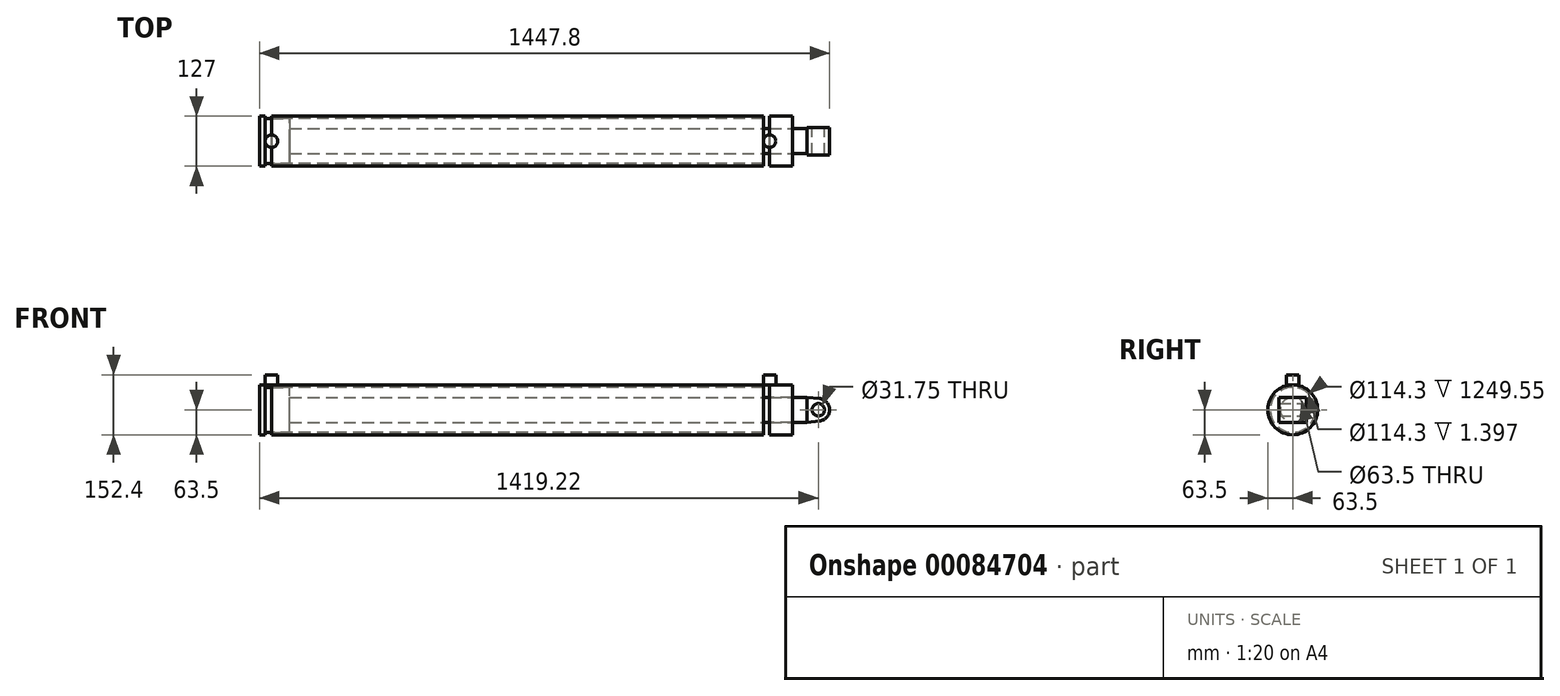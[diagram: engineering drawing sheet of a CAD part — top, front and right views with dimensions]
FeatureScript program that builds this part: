
annotation { "Feature Type Name" : "Feature", "Feature Type Description" : "" }
export const myFeature = defineFeature(function(context is Context, id is Id, definition is map)
    precondition{}
    {
        {
            var Q0;
            Q0=qCreatedBy(makeId("Front.planeOp"),FACE);
            var sketch = newSketch(context, id + "F0", { "sketchPlane" : qUnion([Q0])});
            skLineSegment(sketch, "E0.bottom", {"start": v(0, 0) * mm, "end": v(12.7, 0) * mm});
            skLineSegment(sketch, "E0.top", {"start": v(0, 63.5) * mm, "end": v(1353.31, 63.5) * mm});
            skLineSegment(sketch, "E0.left", {"start": v(0, 0) * mm, "end": v(0, 63.5) * mm});
            skLineSegment(sketch, "E0.right", {"start": v(1353.31, 31.75) * mm, "end": v(1353.31, 63.5) * mm});
            skLineSegment(sketch, "E1", {"start": v(12.7, 0) * mm, "end": v(12.7, 57.15) * mm});
            skLineSegment(sketch, "E2", {"start": v(12.7, 57.15) * mm, "end": v(1295.4, 57.15) * mm});
            skLineSegment(sketch, "E3", {"start": v(1295.4, 57.15) * mm, "end": v(1295.4, 31.75) * mm});
            skLineSegment(sketch, "E4", {"start": v(1295.4, 31.75) * mm, "end": v(1353.31, 31.75) * mm});
            skPoint(sketch, "E5.trimOffspring.start.orphan", {"position": v(1295.4, 0) * mm});
            skLineSegment(sketch, "E6", {"start": v(76.2, 57.15) * mm, "end": v(76.2, 31.75) * mm});
            skLineSegment(sketch, "E7", {"start": v(76.2, 31.75) * mm, "end": v(1390.65, 31.75) * mm});
            skLineSegment(sketch, "E8", {"start": v(1390.65, 31.75) * mm, "end": v(1390.65, 0) * mm});
            skLineSegment(sketch, "E9", {"start": v(1390.65, 0) * mm, "end": v(12.7, 0) * mm});
            skCircle(sketch, "E10", {"center": v(1419.23, 0) * mm, "radius": 28.58 * mm});
            skCircle(sketch, "E11", {"center": v(1419.23, 0) * mm, "radius": 15.88 * mm});
            skLineSegment(sketch, "E12", {"start": v(1422.22, 28.42) * mm, "end": v(1390.65, 31.75) * mm});
            skLineSegment(sketch, "E13", {"start": v(1390.65, 0) * mm, "end": v(1390.65, -31.75) * mm});
            skLineSegment(sketch, "E14", {"start": v(1390.65, -31.75) * mm, "end": v(1422.22, -28.42) * mm});
            skLineSegment(sketch, "E15.bottom", {"start": v(29.97, 57.15) * mm, "end": v(14.1, 57.15) * mm});
            skLineSegment(sketch, "E15.top", {"start": v(29.97, 88.9) * mm, "end": v(14.1, 88.9) * mm});
            skLineSegment(sketch, "E15.left", {"start": v(29.97, 57.15) * mm, "end": v(29.97, 88.9) * mm});
            skLineSegment(sketch, "E15.right", {"start": v(14.1, 57.15) * mm, "end": v(14.1, 88.9) * mm});
            skLineSegment(sketch, "E16.bottom", {"start": v(1279.53, 57.15) * mm, "end": v(1295.4, 57.15) * mm});
            skLineSegment(sketch, "E16.top", {"start": v(1279.53, 88.9) * mm, "end": v(1295.4, 88.9) * mm});
            skLineSegment(sketch, "E16.left", {"start": v(1279.53, 57.15) * mm, "end": v(1279.53, 88.9) * mm});
            skLineSegment(sketch, "E16.right", {"start": v(1295.4, 57.15) * mm, "end": v(1295.4, 88.9) * mm});
            skSolve(sketch);
        }
        {
            var Q0;
            Q0=makeQuery(id+"F0.imprint","IMPRINT",FACE,{"disambiguationData":[TD([[makeQuery(id+"F0.imprint","IMPRINT",EDGE,{"derivedFrom":sQuery(id+"F0.wireOp",EDGE,"E0.bottom")}),1.0]])]});
            var Q1;
            {var subQ5=sQuery(id+"F0.wireOp",EDGE,"E15.bottom");Q1=makeQuery(id+"F0.imprint","IMPRINT",FACE,{"disambiguationData":[TD([[makeQuery(id+"F0.imprint","IMPRINT",EDGE,{"derivedFrom":subQ5}),-1.0]])]});}
            var Q2;
            {var subQ0=sQuery(id+"F0.wireOp",EDGE,"E15.left");var subQ3=sQuery(id+"F0.wireOp",EDGE,"E0.top");var subQ4=makeQuery(id+"F0.imprint","INTERSECT",VERTEX,{"derivedFrom":[subQ3,subQ0]});Q2=makeQuery(id+"F0.imprint","IMPRINT",FACE,{"disambiguationData":[TD([[makeQuery(id+"F0.imprint","IMPRINT",EDGE,{"disambiguationData":[TD([[subQ4,-1.0]])],"derivedFrom":subQ3}),-1.0]])]});}
            var Q3;
            {var subQ5=sQuery(id+"F0.wireOp",EDGE,"E16.bottom");Q3=makeQuery(id+"F0.imprint","IMPRINT",FACE,{"disambiguationData":[TD([[makeQuery(id+"F0.imprint","IMPRINT",EDGE,{"derivedFrom":subQ5}),1.0]])]});}
            var Q4;
            {var subQ1=sQuery(id+"F0.wireOp",EDGE,"E0.right");Q4=makeQuery(id+"F0.imprint","IMPRINT",FACE,{"disambiguationData":[TD([[makeQuery(id+"F0.imprint","IMPRINT",EDGE,{"derivedFrom":subQ1}),1.0]])]});}
            var Q5;
            Q5=sQuery(id+"F0.wireOp",EDGE,"E0.bottom");
            revolve(context, id + "F1", {"entities" : qUnion([Q0, Q1, Q2, Q3, Q4]), "axis" : qUnion([Q5]), "revolveType" : RevolveType.FULL});
        }
        {
            var Q0;
            {var subQ5=sQuery(id+"F0.wireOp",EDGE,"E15.top");Q0=makeQuery(id+"F0.imprint","IMPRINT",FACE,{"disambiguationData":[TD([[makeQuery(id+"F0.imprint","IMPRINT",EDGE,{"derivedFrom":subQ5}),1.0]])]});}
            var Q1;
            {var subQ5=sQuery(id+"F0.wireOp",EDGE,"E15.bottom");Q1=makeQuery(id+"F0.imprint","IMPRINT",FACE,{"disambiguationData":[TD([[makeQuery(id+"F0.imprint","IMPRINT",EDGE,{"derivedFrom":subQ5}),-1.0]])]});}
            var Q2;
            Q2=sQuery(id+"F0.wireOp",EDGE,"E15.left");
            revolve(context, id + "F2", {"operationType" : NewBodyOperationType.ADD, "entities" : qUnion([Q0, Q1]), "axis" : qUnion([Q2]), "revolveType" : RevolveType.FULL});
        }
        {
            var Q0;
            {var subQ5=sQuery(id+"F0.wireOp",EDGE,"E16.top");Q0=makeQuery(id+"F0.imprint","IMPRINT",FACE,{"disambiguationData":[TD([[makeQuery(id+"F0.imprint","IMPRINT",EDGE,{"derivedFrom":subQ5}),-1.0]])]});}
            var Q1;
            {var subQ5=sQuery(id+"F0.wireOp",EDGE,"E16.bottom");Q1=makeQuery(id+"F0.imprint","IMPRINT",FACE,{"disambiguationData":[TD([[makeQuery(id+"F0.imprint","IMPRINT",EDGE,{"derivedFrom":subQ5}),1.0]])]});}
            var Q2;
            Q2=sQuery(id+"F0.wireOp",EDGE,"E16.right");
            revolve(context, id + "F3", {"operationType" : NewBodyOperationType.ADD, "entities" : qUnion([Q0, Q1]), "axis" : qUnion([Q2]), "revolveType" : RevolveType.FULL});
        }
        {
            var Q0;
            {var subQ4=sQuery(id+"F0.wireOp",EDGE,"E1");Q0=makeQuery(id+"F0.imprint","IMPRINT",FACE,{"disambiguationData":[TD([[makeQuery(id+"F0.imprint","IMPRINT",EDGE,{"derivedFrom":subQ4}),-1.0]])]});}
            var Q1;
            Q1=sQuery(id+"F0.wireOp",EDGE,"E9");
            revolve(context, id + "F4", {"entities" : qUnion([Q0]), "axis" : qUnion([Q1]), "revolveType" : RevolveType.FULL});
        }
        {
            var Q0;
            {var subQ0=sQuery(id+"F0.wireOp",EDGE,"E8");Q0=makeQuery(id+"F0.imprint","IMPRINT",FACE,{"disambiguationData":[TD([[makeQuery(id+"F0.imprint","IMPRINT",EDGE,{"derivedFrom":subQ0}),1.0]])]});}
            var Q1;
            Q1=makeQuery(id+"F0.imprint","IMPRINT",FACE,{"disambiguationData":[TD([[makeQuery(id+"F0.imprint","IMPRINT",EDGE,{"derivedFrom":sQuery(id+"F0.wireOp",EDGE,"E11")}),-1.0]])]});
            var Q2;
            {var subQ0=sQuery(id+"F0.wireOp",EDGE,"E13");Q2=makeQuery(id+"F0.imprint","IMPRINT",FACE,{"disambiguationData":[TD([[makeQuery(id+"F0.imprint","IMPRINT",EDGE,{"derivedFrom":subQ0}),1.0]])]});}
            extrude(context, id + "F5", {"entities" : qUnion([Q0, Q1, Q2]), "operationType" : NewBodyOperationType.ADD, "endBound" : BoundingType.SYMMETRIC, "depth" : 69.85 * mm});
        }
    });
